# Revit family: WashBasin-60cm-Vitra_EqualSeries_7241
name_source: partatom
category: Plumbing Fixtures
revit_build: Autodesk Revit 2017 (Build: 20160225_1515(x64)
units: mm (PartAtom-declared; Revit-internal decimal feet)

## family parameters
Cut with Voids When Loaded = No
Host = Face
OmniClass Number = 23.45.05.14.14
OmniClass Title = Sinks/Lavatories
Part Type = Normal
Room Calculation Point = No
Round Connector Dimension = Use Diameter
Shared = Yes

## types (5) — shared parameters
BIMobject category = Sanitary - Basins
Brand = VitrA
CW Connection = No
Default Elevation = 850 mm
Description = VitrA Equal With Tap Hole - With Overflow Hole - 60 cm
Design country = Turkey
HW Connection = No
IFC Classification = Sanitary Terminal
Main Material = Ceramic
Manufacturer = VitrA
Manufacturer name = Vitra
Masterformat 2014 Code = 22 41 16
Masterformat 2014 Description = Residential Lavatories and Sinks
NBS Referans Code = 35-65-70-94
NBS Referans Description = Wash Basin Systems
Nominal Depth (mm) = 450 mm
Nominal Height (mm) = 166 mm
Nominal Width (mm) = 600 mm
OmniClass Code = 23.45.05.14.14
OmniClass Description = Sinks/Lavatories
Primary Material = <By Category>
Product group = Equal
UNSPSC Code = 301815
URL = https://www.vitraglobal.com
Uniclass 1.4 Code = L7212
Uniclass 1.4 Description = Washbasins
Uniclass 2.0 Code = SS-35-65-70-94
Uniclass 2.0 Description = Sanitary Dispensing And Disposal Units
Uniclass 2015 Code = Pr_40_20_96_81
Uniclass 2015 Name = Wash basins Sinks and troughs
Uniformat II Code = D2010
Uniformat II Description = Plumbing Fixtures
Vent Connection = No
Warranty Period (Year) = 10 Years
Waste Connection = Yes
Weight Net (kg) = 21.8
Youtube = https://www.youtube.com

## per-type parameters (varying)
| type | Article No. (default) | Color | Model | Mounting type | Product SKU | Product certification | Product data url | Product family | Product url | Secondary Material | Technical description |
| WashBasin-Countertop-Vitra_EqualSeries_7241B476-0631 | 7241B476-0631 | Stone Grey | 7241B476-0631 | Countertop | 7241B476-0631 | https://vitraglobal.com | https://www.vitraglobal.com | Countertop WashBasin |  | Stone Grey | https://www.vitraglobal.com |
| WashBasin-Vitra_EqualSeries_7241B476-0001 | 7241B476-0001 | Stone Grey | 7241B476-0001 | Wall Mounted | 7241B476-0001 | https://www.vitraglobal.com | https://www.vitraglobal.com | Wall Mounted WashBasin |  | Stone Grey | https://www.vitraglobal.com |
| WashBasin-Countertop-Vitra_EqualSeries_7241B403-0631 | 7241B403-0631 | White | 7241B403-0631 | Countertop | 7241B403-0631 | https://vitraglobal.com | https://www.vitraglobal.com | Countertop WashBasin |  | White | https://www.vitraglobal.com |
| WashBasin-Vitra_EqualSeries_7241B403-0001 | 7241B403-0001 | White | 7241B403-0001 | Wall Mounted | 7241B403-0001 | https://www.vitraglobal.com | https://www.bimobject.com | Wall Mounted WashBasin | https://www.vitraglobal.com | White | https://www.vitraglobal.com |
| WashBasin-Countertop-Vitra_EqualSeries_7241B403H0631 | 7241B403H0631 | White | 7241B403H0631 | Countertop | 7241B403H0631 | https://vitraglobal.com |  | Countertop WashBasin | https://www.vitra-india.com | White | https://www.vitra-india.com |

## geometry (parser evidence)
native form markers: Sweep x2
no freeform markers — native parametric forms only
